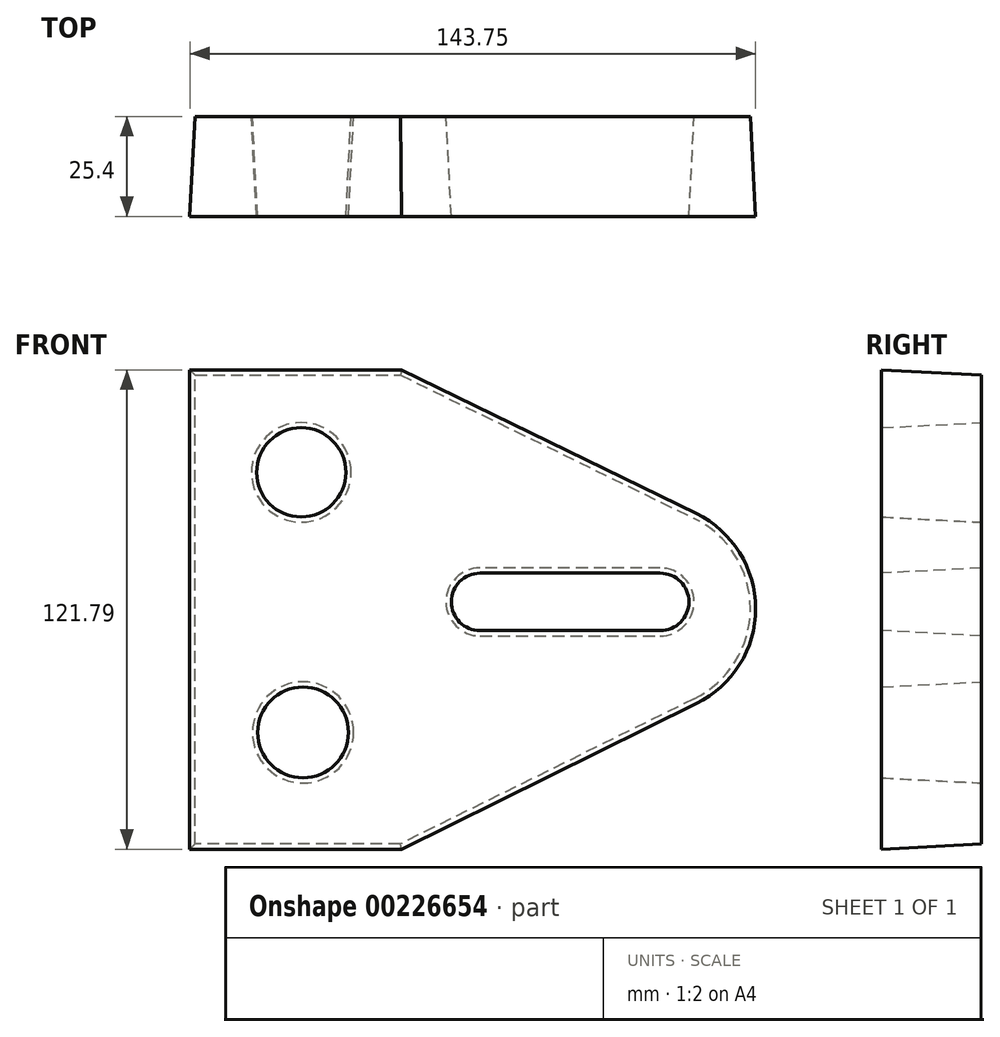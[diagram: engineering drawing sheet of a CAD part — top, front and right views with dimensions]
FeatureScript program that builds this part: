
annotation { "Feature Type Name" : "Feature", "Feature Type Description" : "" }
export const myFeature = defineFeature(function(context is Context, id is Id, definition is map)
    precondition{}
    {
        {
            var Q0;
            Q0=qCreatedBy(makeId("Front.planeOp"),FACE);
            var sketch = newSketch(context, id + "F0", { "sketchPlane" : qUnion([Q0])});
            skLineSegment(sketch, "E0", {"start": v(-72.4, 57.09) * mm, "end": v(-72.4, -62.03) * mm});
            skLineSegment(sketch, "E1", {"start": v(-72.4, -62.03) * mm, "end": v(-20.26, -62.03) * mm});
            skLineSegment(sketch, "E2", {"start": v(-72.4, 57.09) * mm, "end": v(-20.26, 57.09) * mm});
            skLineSegment(sketch, "E3", {"start": v(-20.26, 57.09) * mm, "end": v(54.36, 20.68) * mm});
            skLineSegment(sketch, "E4", {"start": v(-20.26, -62.03) * mm, "end": v(54.36, -25.17) * mm});
            skArc(sketch, "E5", {"start": v(54.36, 20.68) * mm, "mid": v(68.69, -2.25) * mm, "end": v(54.36, -25.17) * mm});
            skCircle(sketch, "E6", {"center": v(-45.43, 32.36) * mm, "radius": 12.67 * mm});
            skCircle(sketch, "E7", {"center": v(-44.98, -33.71) * mm, "radius": 12.86 * mm});
            skLineSegment(sketch, "E8", {"start": v(0, 8.09) * mm, "end": v(45.76, 8.09) * mm});
            skLineSegment(sketch, "E9", {"start": v(0, -9.19) * mm, "end": v(45.76, -9.19) * mm});
            skArc(sketch, "E10", {"start": v(45.76, 8.09) * mm, "mid": v(54.4, -0.55) * mm, "end": v(45.76, -9.19) * mm});
            skArc(sketch, "E11", {"start": v(0, 8.09) * mm, "mid": v(-8.64, -0.55) * mm, "end": v(0, -9.19) * mm});
            skSolve(sketch);
        }
        {
            var Q0;
            Q0 = qSketchRegion(id + "F0", true);
            extrude(context, id + "F1", {"entities" : qUnion([Q0]), "depth" : 25.4 * mm, "hasDraft" : true, "draftAngle" : 3 * degree});
        }
    });
